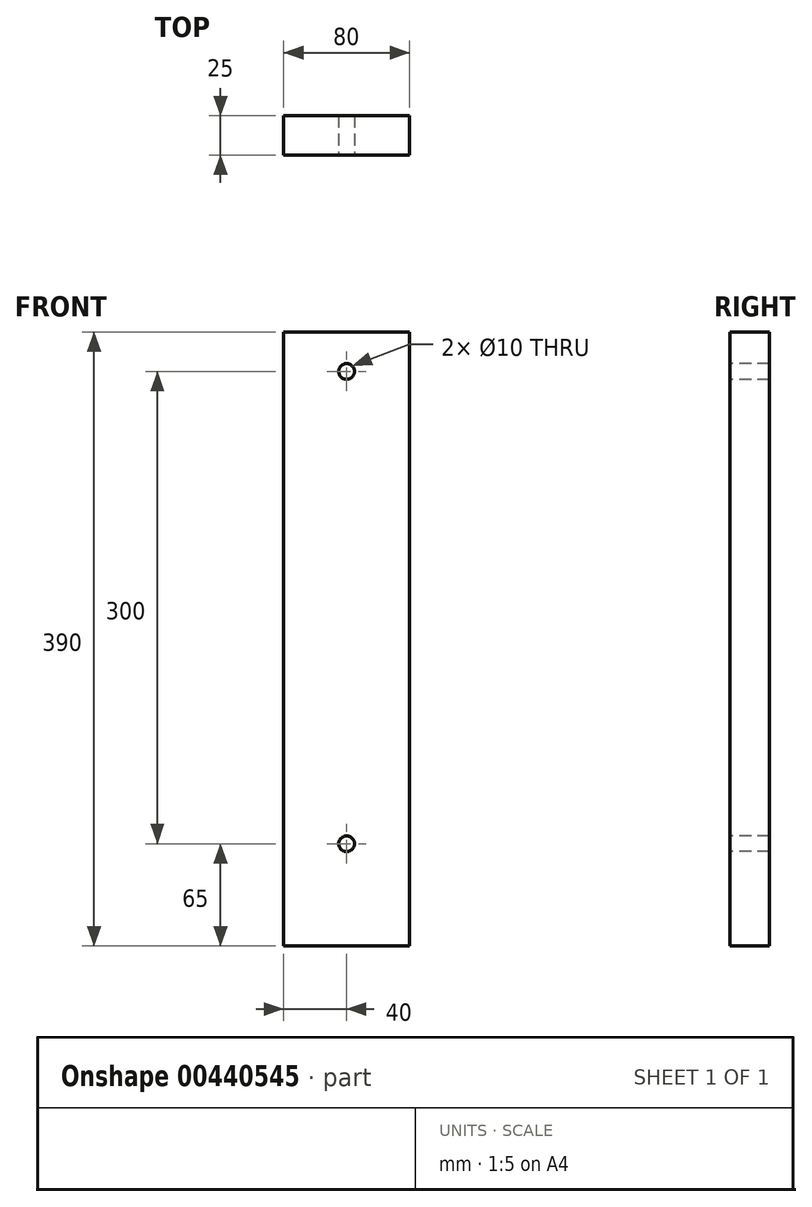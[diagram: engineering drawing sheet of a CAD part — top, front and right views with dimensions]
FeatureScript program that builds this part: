
annotation { "Feature Type Name" : "Feature", "Feature Type Description" : "" }
export const myFeature = defineFeature(function(context is Context, id is Id, definition is map)
    precondition{}
    {
        {
            var Q0;
            Q0=qCreatedBy(makeId("Front.planeOp"),FACE);
            var sketch = newSketch(context, id + "F0", { "sketchPlane" : qUnion([Q0])});
            skLineSegment(sketch, "E0.bottom", {"start": v(-40, 195) * mm, "end": v(40, 195) * mm});
            skLineSegment(sketch, "E0.top", {"start": v(-40, -195) * mm, "end": v(40, -195) * mm});
            skLineSegment(sketch, "E0.left", {"start": v(-40, 195) * mm, "end": v(-40, -195) * mm});
            skLineSegment(sketch, "E0.right", {"start": v(40, 195) * mm, "end": v(40, -195) * mm});
            skPoint(sketch, "E0.middle", {"position": v(0, 0) * mm});
            skLineSegment(sketch, "E1", {"start": v(0, -195) * mm, "end": v(0, 195) * mm});
            skLineSegment(sketch, "E2", {"start": v(-40, -130) * mm, "end": v(40, -130) * mm});
            skLineSegment(sketch, "E3", {"start": v(-40, 170) * mm, "end": v(40, 170) * mm});
            skPoint(sketch, "E4", {"position": v(0, 170) * mm});
            skPoint(sketch, "E5", {"position": v(0, -130) * mm});
            skSolve(sketch);
        }
        {
            var Q0;
            {var subQ0=sQuery(id+"F0.wireOp",EDGE,"E2");var subQ1=sQuery(id+"F0.wireOp",EDGE,"E0.left");var subQ2=makeQuery(id+"F0.imprint","INTERSECT",VERTEX,{"derivedFrom":[subQ1,subQ0]});Q0=makeQuery(id+"F0.imprint","IMPRINT",FACE,{"disambiguationData":[TD([[makeQuery(id+"F0.imprint","IMPRINT",EDGE,{"disambiguationData":[TD([[subQ2,1.0]])],"derivedFrom":subQ1}),1.0]])]});}
            var Q1;
            {var subQ0=sQuery(id+"F0.wireOp",EDGE,"E2");var subQ1=sQuery(id+"F0.wireOp",EDGE,"E0.right");var subQ2=makeQuery(id+"F0.imprint","INTERSECT",VERTEX,{"derivedFrom":[subQ1,subQ0]});Q1=makeQuery(id+"F0.imprint","IMPRINT",FACE,{"disambiguationData":[TD([[makeQuery(id+"F0.imprint","IMPRINT",EDGE,{"disambiguationData":[TD([[subQ2,1.0]])],"derivedFrom":subQ1}),-1.0]])]});}
            var Q2;
            {var subQ0=sQuery(id+"F0.wireOp",EDGE,"E0.right");var subQ1=sQuery(id+"F0.wireOp",EDGE,"E0.bottom");var subQ2=makeQuery(id+"F0.imprint","INTERSECT",VERTEX,{"derivedFrom":[subQ1,subQ0]});Q2=makeQuery(id+"F0.imprint","IMPRINT",FACE,{"disambiguationData":[TD([[makeQuery(id+"F0.imprint","IMPRINT",EDGE,{"disambiguationData":[TD([[subQ2,1.0]])],"derivedFrom":subQ1}),-1.0]])]});}
            var Q3;
            {var subQ0=sQuery(id+"F0.wireOp",EDGE,"E0.left");var subQ1=sQuery(id+"F0.wireOp",EDGE,"E0.bottom");var subQ2=makeQuery(id+"F0.imprint","INTERSECT",VERTEX,{"derivedFrom":[subQ1,subQ0]});Q3=makeQuery(id+"F0.imprint","IMPRINT",FACE,{"disambiguationData":[TD([[makeQuery(id+"F0.imprint","IMPRINT",EDGE,{"disambiguationData":[TD([[subQ2,-1.0]])],"derivedFrom":subQ1}),-1.0]])]});}
            var Q4;
            {var subQ0=sQuery(id+"F0.wireOp",EDGE,"E0.right");var subQ1=sQuery(id+"F0.wireOp",EDGE,"E0.top");var subQ2=makeQuery(id+"F0.imprint","INTERSECT",VERTEX,{"derivedFrom":[subQ1,subQ0]});Q4=makeQuery(id+"F0.imprint","IMPRINT",FACE,{"disambiguationData":[TD([[makeQuery(id+"F0.imprint","IMPRINT",EDGE,{"disambiguationData":[TD([[subQ2,1.0]])],"derivedFrom":subQ1}),1.0]])]});}
            var Q5;
            {var subQ0=sQuery(id+"F0.wireOp",EDGE,"E0.left");var subQ1=sQuery(id+"F0.wireOp",EDGE,"E0.top");var subQ2=makeQuery(id+"F0.imprint","INTERSECT",VERTEX,{"derivedFrom":[subQ1,subQ0]});Q5=makeQuery(id+"F0.imprint","IMPRINT",FACE,{"disambiguationData":[TD([[makeQuery(id+"F0.imprint","IMPRINT",EDGE,{"disambiguationData":[TD([[subQ2,-1.0]])],"derivedFrom":subQ1}),1.0]])]});}
            extrude(context, id + "F1", {"entities" : qUnion([Q0, Q1, Q2, Q3, Q4, Q5]), "oppositeDirection" : true, "depth" : 25 * mm});
        }
        {
            var Q0;
            Q0=sQuery(id+"F0.wireOp",VERTEX,"E4");
            var Q1;
            Q1=sQuery(id+"F0.wireOp",VERTEX,"E5");
            var Q2;
            Q2=makeQuery(id+"F1.opExtrude","SWEPT_BODY",BODY,{"disambiguationData":[OSD([sQuery(id+"F0.wireOp",EDGE,"E0.bottom"),sQuery(id+"F0.wireOp",EDGE,"E0.top"),sQuery(id+"F0.wireOp",EDGE,"E0.left"),sQuery(id+"F0.wireOp",EDGE,"E0.right")])]});
            hole(context, id + "F2", {"style" : HoleStyle.SIMPLE, "endStyle" : HoleEndStyle.THROUGH, "holeDiameter" : 10 * mm, "isTappedThrough" : true, "tappedDepth" : 12 * mm, "tapClearance" : 3, "startFromSketch" : true, "locations" : qUnion([Q0, Q1]), "scope" : qUnion([Q2])});
        }
    });
